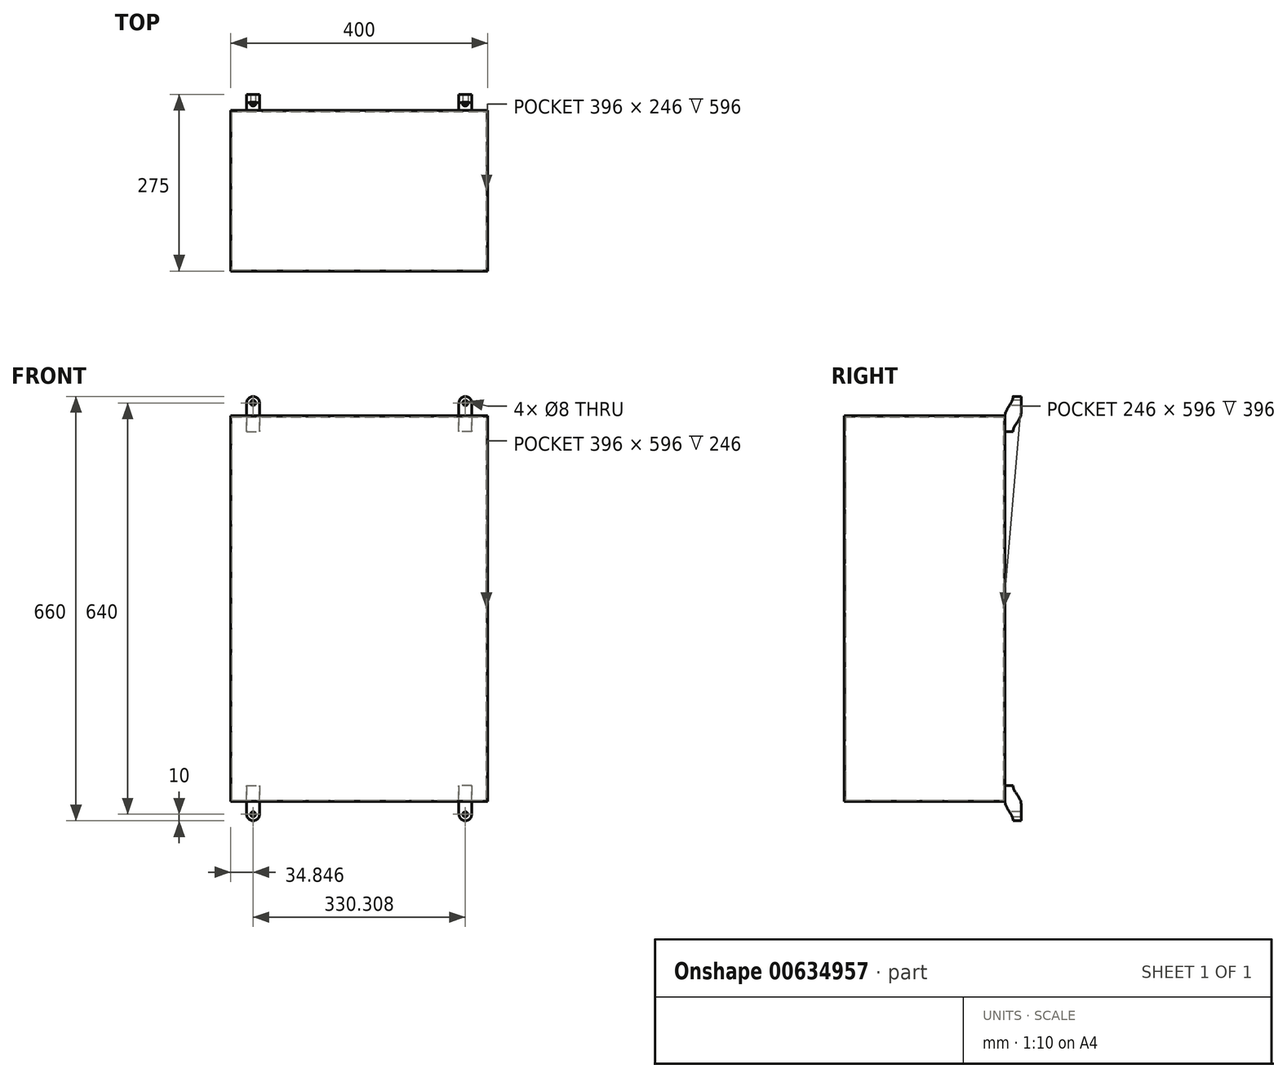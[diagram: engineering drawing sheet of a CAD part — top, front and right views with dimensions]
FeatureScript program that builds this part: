
annotation { "Feature Type Name" : "Feature", "Feature Type Description" : "" }
export const myFeature = defineFeature(function(context is Context, id is Id, definition is map)
    precondition{}
    {
        {
            var Q0;
            Q0=qCreatedBy(makeId("Front.planeOp"),FACE);
            var sketch = newSketch(context, id + "F0", { "sketchPlane" : qUnion([Q0])});
            skLineSegment(sketch, "E0.bottom", {"start": v(-200, -300) * mm, "end": v(200, -300) * mm});
            skLineSegment(sketch, "E0.top", {"start": v(-200, 300) * mm, "end": v(200, 300) * mm});
            skLineSegment(sketch, "E0.left", {"start": v(-200, -300) * mm, "end": v(-200, 300) * mm});
            skLineSegment(sketch, "E0.right", {"start": v(200, -300) * mm, "end": v(200, 300) * mm});
            skPoint(sketch, "E0.middle", {"position": v(0, 0) * mm});
            skSolve(sketch);
        }
        {
            var Q0;
            Q0 = qSketchRegion(id + "F0", true);
            extrude(context, id + "F1", {"entities" : qUnion([Q0]), "endBound" : BoundingType.SYMMETRIC, "depth" : 250 * mm, "offsetDistance" : 25 * mm});
        }
        {
            var Q0;
            Q0=makeQuery(id+"F1.opExtrude","SWEPT_FACE",FACE,{"disambiguationData":[OSD([sQuery(id+"F0.wireOp",EDGE,"E0.top")])]});
            var Q1;
            Q1=makeQuery(id+"F1.opExtrude","SWEPT_BODY",BODY,{"disambiguationData":[OSD([sQuery(id+"F0.wireOp",EDGE,"E0.bottom"),sQuery(id+"F0.wireOp",EDGE,"E0.top"),sQuery(id+"F0.wireOp",EDGE,"E0.left"),sQuery(id+"F0.wireOp",EDGE,"E0.right")])]});
            shell(context, id + "F2", {"isHollow" : true, "entities" : qUnion([Q0]), "parts" : qUnion([Q1]), "thickness" : 2 * mm});
        }
        {
            var Q0;
            Q0=makeQuery(id+"F1.opExtrude","CAP_FACE",FACE,{"disambiguationData":[OSD([sQuery(id+"F0.wireOp",EDGE,"E0.bottom"),sQuery(id+"F0.wireOp",EDGE,"E0.top"),sQuery(id+"F0.wireOp",EDGE,"E0.left"),sQuery(id+"F0.wireOp",EDGE,"E0.right")])],"isStart":true});
            var sketch = newSketch(context, id + "F3", { "sketchPlane" : qUnion([Q0])});
            skLineSegment(sketch, "E1", {"start": v(-165.15, 357.53) * mm, "end": v(-165.15, -316.5) * mm, "construction": true});
            skLineSegment(sketch, "E2", {"start": v(0, 343.43) * mm, "end": v(0, -316.5) * mm, "construction": true});
            skCircle(sketch, "E3", {"center": v(-165.15, 320) * mm, "radius": 4 * mm});
            skArc(sketch, "E4", {"start": v(-155.15, 320) * mm, "mid": v(-165.15, 330) * mm, "end": v(-175.15, 320) * mm});
            skLineSegment(sketch, "E5", {"start": v(-180.47, 320) * mm, "end": v(-150.07, 320) * mm, "construction": true});
            skLineSegment(sketch, "E6.bottom", {"start": v(-175.15, 320) * mm, "end": v(-155.15, 320) * mm});
            skLineSegment(sketch, "E6.top", {"start": v(-175.15, 275) * mm, "end": v(-155.15, 275) * mm});
            skLineSegment(sketch, "E6.left", {"start": v(-175.15, 320) * mm, "end": v(-175.15, 275) * mm});
            skLineSegment(sketch, "E6.right", {"start": v(-155.15, 320) * mm, "end": v(-155.15, 275) * mm});
            skLineSegment(sketch, "E7", {"start": v(-273.34, 0) * mm, "end": v(310.36, 0) * mm, "construction": true});
            skLineSegment(sketch, "E8.MirrorCS", {"start": v(-155.15, -320) * mm, "end": v(-155.15, -275) * mm});
            skArc(sketch, "E9.MirrorCS", {"start": v(-155.15, -320) * mm, "mid": v(-165.15, -330) * mm, "end": v(-175.15, -320) * mm});
            skCircle(sketch, "E10.MirrorC", {"center": v(-165.15, -320) * mm, "radius": 4 * mm});
            skLineSegment(sketch, "E11.MirrorCS", {"start": v(-175.15, -320) * mm, "end": v(-175.15, -275) * mm});
            skLineSegment(sketch, "E12.MirrorCS", {"start": v(-175.15, -275) * mm, "end": v(-155.15, -275) * mm});
            skLineSegment(sketch, "E13.MirrorCS", {"start": v(175.15, 320) * mm, "end": v(155.15, 320) * mm});
            skLineSegment(sketch, "E14.MirrorCS", {"start": v(180.47, 320) * mm, "end": v(150.07, 320) * mm, "construction": true});
            skCircle(sketch, "E15.MirrorC", {"center": v(165.15, 320) * mm, "radius": 4 * mm});
            skArc(sketch, "E16.MirrorCS", {"start": v(155.15, 320) * mm, "mid": v(165.15, 330) * mm, "end": v(175.15, 320) * mm});
            skLineSegment(sketch, "E17.MirrorCS", {"start": v(175.15, 275) * mm, "end": v(155.15, 275) * mm});
            skLineSegment(sketch, "E18.MirrorCS", {"start": v(155.15, 320) * mm, "end": v(155.15, 275) * mm});
            skLineSegment(sketch, "E19.MirrorCS", {"start": v(175.15, 320) * mm, "end": v(175.15, 275) * mm});
            skLineSegment(sketch, "E20.MirrorCS", {"start": v(175.15, -275) * mm, "end": v(155.15, -275) * mm});
            skLineSegment(sketch, "E21.MirrorCS", {"start": v(175.15, -320) * mm, "end": v(175.15, -275) * mm});
            skCircle(sketch, "E22.MirrorC", {"center": v(165.15, -320) * mm, "radius": 4 * mm});
            skArc(sketch, "E23.MirrorCS", {"start": v(155.15, -320) * mm, "mid": v(165.15, -330) * mm, "end": v(175.15, -320) * mm});
            skLineSegment(sketch, "E24.MirrorCS", {"start": v(155.15, -320) * mm, "end": v(155.15, -275) * mm});
            skSolve(sketch);
        }
        {
            var Q0;
            Q0 = qSketchRegion(id + "F3", true);
            extrude(context, id + "F4", {"entities" : qUnion([Q0]), "operationType" : NewBodyOperationType.ADD, "depth" : 25 * mm, "offsetDistance" : 25 * mm});
        }
        {
            var Q0;
            Q0=makeQuery(id+"F4.opExtrude","SWEPT_FACE",FACE,{"disambiguationData":[OSD([sQuery(id+"F3.wireOp",EDGE,"E6.left")])]});
            var sketch = newSketch(context, id + "F5", { "sketchPlane" : qUnion([Q0])});
            skLineSegment(sketch, "E25", {"start": v(125, 330) * mm, "end": v(137.5, 330) * mm});
            skLineSegment(sketch, "E26.0", {"start": v(150, 275) * mm, "end": v(137.5, 275) * mm});
            skLineSegment(sketch, "E27", {"start": v(137.5, 330) * mm, "end": v(137.5, 338.77) * mm, "construction": true});
            skLineSegment(sketch, "E28", {"start": v(137.5, 275) * mm, "end": v(137.5, 262.85) * mm, "construction": true});
            skFitSpline(sketch, "E29", {"points": [v(137.5, 275) * mm, v(150, 303.7) * mm], "startDerivative": vector(0, 31.3) * mm, "endDerivative": vector(0, 31.3) * mm});
            skLineSegment(sketch, "E30.0", {"start": v(150, 320) * mm, "end": v(150, 303.7) * mm, "construction": true});
            skFitSpline(sketch, "E31", {"points": [v(125, 300) * mm, v(137.5, 330) * mm], "startDerivative": vector(0, 32.5) * mm, "endDerivative": vector(0, 32.5) * mm});
            skLineSegment(sketch, "E32.0", {"start": v(125, 300) * mm, "end": v(125, 275) * mm, "construction": true});
            skPoint(sketch, "E33.orphan", {"position": v(150, 330) * mm});
            skLineSegment(sketch, "E34", {"start": v(125, 330) * mm, "end": v(125, 300) * mm});
            skLineSegment(sketch, "E35", {"start": v(150, 275) * mm, "end": v(150, 303.7) * mm});
            skLineSegment(sketch, "E36", {"start": v(-181.32, 0) * mm, "end": v(176.93, 0) * mm, "construction": true});
            skFitSpline(sketch, "E37.MirrorCS", {"points": [v(137.5, -275) * mm, v(150, -303.7) * mm], "startDerivative": vector(0, -31.3) * mm, "endDerivative": vector(0, -31.3) * mm});
            skFitSpline(sketch, "E38.MirrorCS", {"points": [v(125, -300) * mm, v(137.5, -330) * mm], "startDerivative": vector(0, -32.5) * mm, "endDerivative": vector(0, -32.5) * mm});
            skLineSegment(sketch, "E39.MirrorCS", {"start": v(150, -275) * mm, "end": v(150, -303.7) * mm});
            skPoint(sketch, "E40.MirrorP", {"position": v(150, -330) * mm});
            skLineSegment(sketch, "E41.MirrorCS", {"start": v(125, -330) * mm, "end": v(125, -300) * mm});
            skLineSegment(sketch, "E42.MirrorCS", {"start": v(125, -330) * mm, "end": v(137.5, -330) * mm});
            skLineSegment(sketch, "E43.MirrorCS", {"start": v(150, -275) * mm, "end": v(137.5, -275) * mm});
            skLineSegment(sketch, "E44.MirrorCS", {"start": v(125, -300) * mm, "end": v(125, -275) * mm, "construction": true});
            skLineSegment(sketch, "E45.MirrorCS", {"start": v(150, -320) * mm, "end": v(150, -303.7) * mm, "construction": true});
            skSolve(sketch);
        }
        {
            var Q0;
            Q0 = qSketchRegion(id + "F5", true);
            var Q1;
            Q1=makeQuery(id+"F4.opExtrude","SWEPT_FACE",FACE,{"disambiguationData":[OSD([sQuery(id+"F3.wireOp",EDGE,"E19.MirrorCS")])]});
            extrude(context, id + "F6", {"entities" : qUnion([Q0]), "operationType" : NewBodyOperationType.REMOVE, "endBound" : BoundingType.UP_TO_SURFACE, "oppositeDirection" : true, "depth" : 25 * mm, "endBoundEntityFace" : qUnion([Q1]), "offsetDistance" : 25 * mm});
        }
    });
